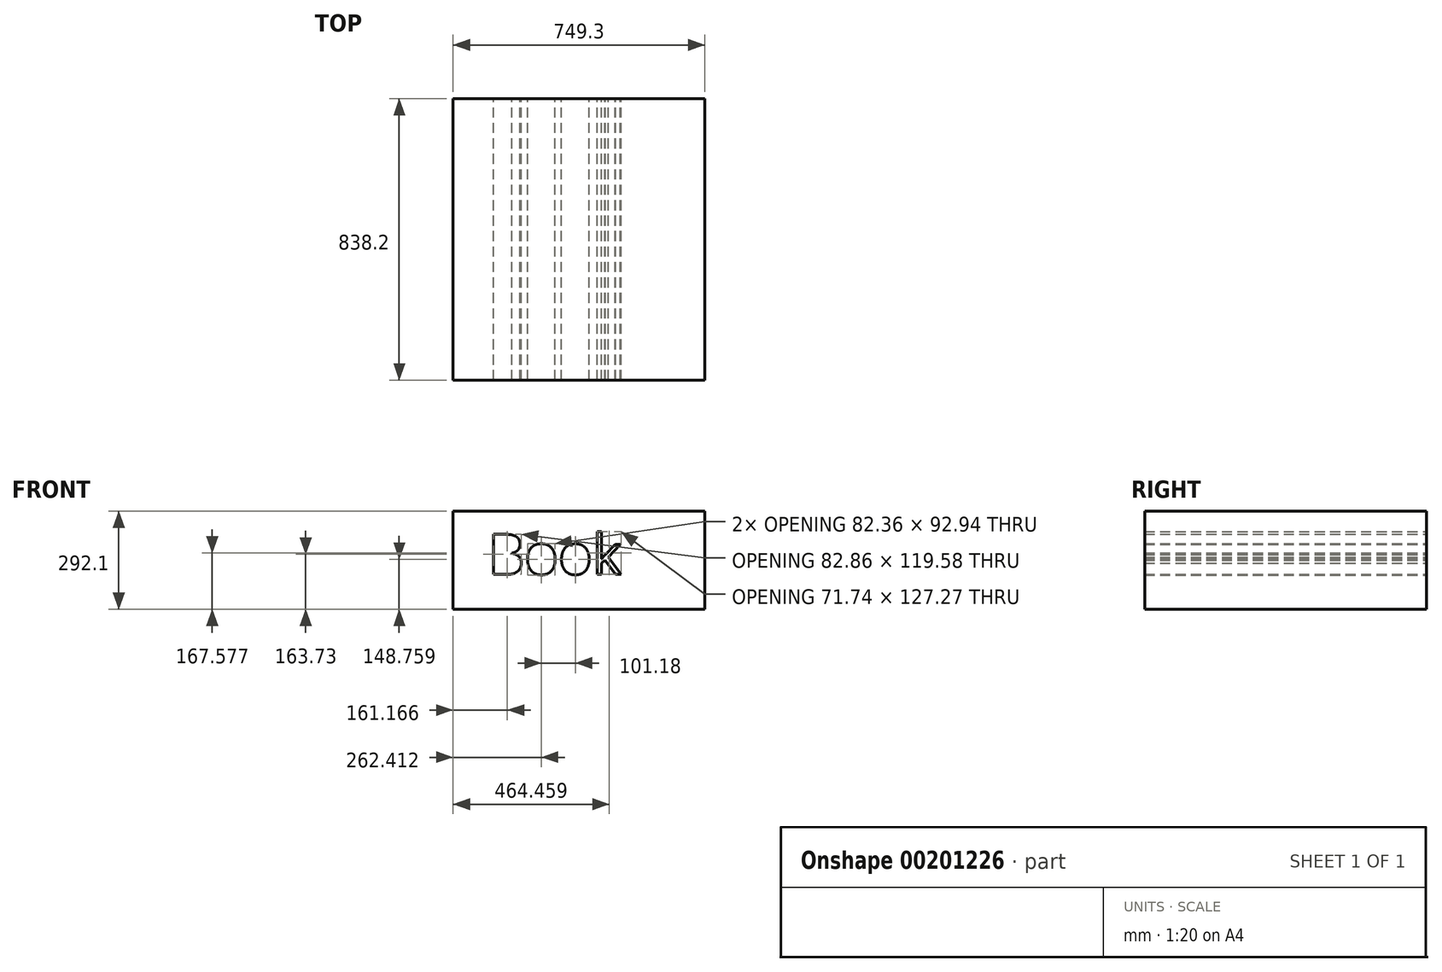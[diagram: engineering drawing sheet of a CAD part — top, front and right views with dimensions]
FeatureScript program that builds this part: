
annotation { "Feature Type Name" : "Feature", "Feature Type Description" : "" }
export const myFeature = defineFeature(function(context is Context, id is Id, definition is map)
    precondition{}
    {
        {
            var Q0;
            Q0=qCreatedBy(makeId("Front.planeOp"),FACE);
            var sketch = newSketch(context, id + "F0", { "sketchPlane" : qUnion([Q0])});
            skLineSegment(sketch, "E0.bottom", {"start": v(-436.02, 92.86) * mm, "end": v(313.28, 92.86) * mm});
            skLineSegment(sketch, "E0.top", {"start": v(-436.02, -199.24) * mm, "end": v(313.28, -199.24) * mm});
            skLineSegment(sketch, "E0.left", {"start": v(-436.02, 92.86) * mm, "end": v(-436.02, -199.24) * mm});
            skLineSegment(sketch, "E0.right", {"start": v(313.28, 92.86) * mm, "end": v(313.28, -199.24) * mm});
            skText(sketch, "E1", { "text": "Book", "fontName": "OpenSans-Regular.ttf"});
            const initialGuessF0  = {"E1": [-0.33272, -0.0953, 1, 0, 0.1206]};
            skSetInitialGuess(sketch, initialGuessF0);
            skSolve(sketch);
        }
        {
            var Q0;
            Q0 = qSketchRegion(id + "F0", true);
            extrude(context, id + "F1", {"entities" : qUnion([Q0]), "depth" : 838.2 * mm});
        }
    });
